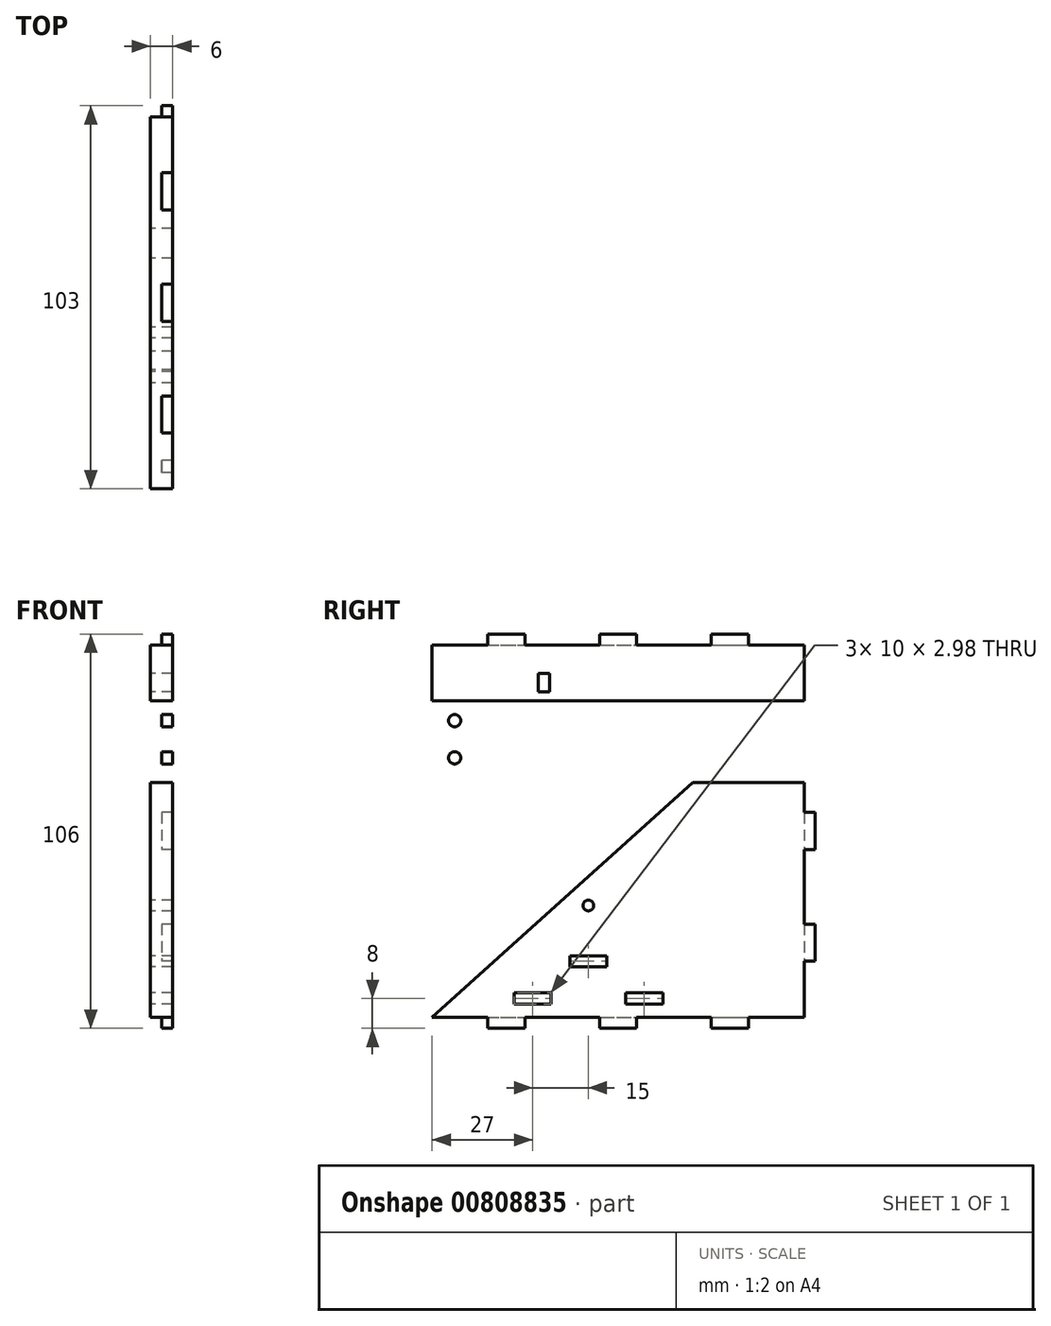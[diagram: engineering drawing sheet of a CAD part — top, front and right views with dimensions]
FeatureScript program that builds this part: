
annotation { "Feature Type Name" : "Feature", "Feature Type Description" : "" }
export const myFeature = defineFeature(function(context is Context, id is Id, definition is map)
    precondition{}
    {
        {
            var Q0;
            Q0=qCreatedBy(makeId("Right.planeOp"),FACE);
            var sketch = newSketch(context, id + "F0", { "sketchPlane" : qUnion([Q0])});
            skLineSegment(sketch, "E0.bottom", {"start": v(-50, 50) * mm, "end": v(50, 50) * mm});
            skLineSegment(sketch, "E0.top", {"start": v(-50, -50) * mm, "end": v(50, -50) * mm});
            skLineSegment(sketch, "E0.left", {"start": v(-50, 50) * mm, "end": v(-50, -50) * mm});
            skLineSegment(sketch, "E0.right", {"start": v(50, 50) * mm, "end": v(50, -50) * mm});
            skPoint(sketch, "E0.middle", {"position": v(0, 0) * mm});
            skLineSegment(sketch, "E1.bottom", {"start": v(-5, 47) * mm, "end": v(5, 47) * mm});
            skLineSegment(sketch, "E1.top", {"start": v(-5, 53) * mm, "end": v(5, 53) * mm});
            skLineSegment(sketch, "E1.left", {"start": v(-5, 47) * mm, "end": v(-5, 53) * mm});
            skLineSegment(sketch, "E1.right", {"start": v(5, 47) * mm, "end": v(5, 53) * mm});
            skPoint(sketch, "E1.middle", {"position": v(0, 50) * mm});
            skLineSegment(sketch, "E2.bottom", {"start": v(35, 53) * mm, "end": v(25, 53) * mm});
            skLineSegment(sketch, "E2.top", {"start": v(35, 47) * mm, "end": v(25, 47) * mm});
            skLineSegment(sketch, "E2.left", {"start": v(35, 53) * mm, "end": v(35, 47) * mm});
            skLineSegment(sketch, "E2.right", {"start": v(25, 53) * mm, "end": v(25, 47) * mm});
            skPoint(sketch, "E2.middle", {"position": v(30, 50) * mm});
            skLineSegment(sketch, "E3.bottom", {"start": v(-35, 53) * mm, "end": v(-25, 53) * mm});
            skLineSegment(sketch, "E3.top", {"start": v(-35, 47) * mm, "end": v(-25, 47) * mm});
            skLineSegment(sketch, "E3.left", {"start": v(-35, 53) * mm, "end": v(-35, 47) * mm});
            skLineSegment(sketch, "E3.right", {"start": v(-25, 53) * mm, "end": v(-25, 47) * mm});
            skPoint(sketch, "E3.middle", {"position": v(-30, 50) * mm});
            skLineSegment(sketch, "E4.1.0", {"start": v(-53, 25) * mm, "end": v(-47, 25) * mm});
            skLineSegment(sketch, "E4.1.1", {"start": v(-53, 35) * mm, "end": v(-53, 25) * mm});
            skLineSegment(sketch, "E4.1.2", {"start": v(-53, 35) * mm, "end": v(-47, 35) * mm});
            skLineSegment(sketch, "E4.1.3", {"start": v(-47, 35) * mm, "end": v(-47, 25) * mm});
            skLineSegment(sketch, "E4.1.4", {"start": v(-47, -5) * mm, "end": v(-47, 5) * mm});
            skLineSegment(sketch, "E4.1.5", {"start": v(-47, 5) * mm, "end": v(-53, 5) * mm});
            skLineSegment(sketch, "E4.1.6", {"start": v(-53, -5) * mm, "end": v(-53, 5) * mm});
            skLineSegment(sketch, "E4.1.7", {"start": v(-47, -5) * mm, "end": v(-53, -5) * mm});
            skLineSegment(sketch, "E4.1.8", {"start": v(-53, -35) * mm, "end": v(-53, -25) * mm});
            skLineSegment(sketch, "E4.1.9", {"start": v(-47, -35) * mm, "end": v(-47, -25) * mm});
            skLineSegment(sketch, "E4.1.10", {"start": v(-53, -25) * mm, "end": v(-47, -25) * mm});
            skLineSegment(sketch, "E4.1.11", {"start": v(-53, -35) * mm, "end": v(-47, -35) * mm});
            skLineSegment(sketch, "E4.2.0", {"start": v(-25, -53) * mm, "end": v(-25, -47) * mm});
            skLineSegment(sketch, "E4.2.1", {"start": v(-35, -53) * mm, "end": v(-25, -53) * mm});
            skLineSegment(sketch, "E4.2.2", {"start": v(-35, -53) * mm, "end": v(-35, -47) * mm});
            skLineSegment(sketch, "E4.2.3", {"start": v(-35, -47) * mm, "end": v(-25, -47) * mm});
            skLineSegment(sketch, "E4.2.4", {"start": v(5, -47) * mm, "end": v(-5, -47) * mm});
            skLineSegment(sketch, "E4.2.5", {"start": v(-5, -47) * mm, "end": v(-5, -53) * mm});
            skLineSegment(sketch, "E4.2.6", {"start": v(5, -53) * mm, "end": v(-5, -53) * mm});
            skLineSegment(sketch, "E4.2.7", {"start": v(5, -47) * mm, "end": v(5, -53) * mm});
            skLineSegment(sketch, "E4.2.8", {"start": v(35, -53) * mm, "end": v(25, -53) * mm});
            skLineSegment(sketch, "E4.2.9", {"start": v(35, -47) * mm, "end": v(25, -47) * mm});
            skLineSegment(sketch, "E4.2.10", {"start": v(25, -53) * mm, "end": v(25, -47) * mm});
            skLineSegment(sketch, "E4.2.11", {"start": v(35, -53) * mm, "end": v(35, -47) * mm});
            skLineSegment(sketch, "E4.3.0", {"start": v(53, -25) * mm, "end": v(47, -25) * mm});
            skLineSegment(sketch, "E4.3.1", {"start": v(53, -35) * mm, "end": v(53, -25) * mm});
            skLineSegment(sketch, "E4.3.2", {"start": v(53, -35) * mm, "end": v(47, -35) * mm});
            skLineSegment(sketch, "E4.3.3", {"start": v(47, -35) * mm, "end": v(47, -25) * mm});
            skLineSegment(sketch, "E4.3.4", {"start": v(47, 5) * mm, "end": v(47, -5) * mm});
            skLineSegment(sketch, "E4.3.5", {"start": v(47, -5) * mm, "end": v(53, -5) * mm});
            skLineSegment(sketch, "E4.3.6", {"start": v(53, 5) * mm, "end": v(53, -5) * mm});
            skLineSegment(sketch, "E4.3.7", {"start": v(47, 5) * mm, "end": v(53, 5) * mm});
            skLineSegment(sketch, "E4.3.8", {"start": v(53, 35) * mm, "end": v(53, 25) * mm});
            skLineSegment(sketch, "E4.3.9", {"start": v(47, 35) * mm, "end": v(47, 25) * mm});
            skLineSegment(sketch, "E4.3.10", {"start": v(53, 25) * mm, "end": v(47, 25) * mm});
            skLineSegment(sketch, "E4.3.11", {"start": v(53, 35) * mm, "end": v(47, 35) * mm});
            skCircle(sketch, "E5", {"center": v(-8, -20) * mm, "radius": 1.45 * mm});
            skSolve(sketch);
        }
        {
            var Q0;
            Q0=qSketchRegion(id+"F0",true);
            extrude(context, id + "F1", {"entities" : qUnion([Q0]), "depth" : 3 * mm, "offsetDistance" : 25 * mm});
        }
        {
            var Q0;
            Q0=makeQuery(id+"F1.opExtrude","CAP_FACE",FACE,{"disambiguationData":[OSD([sQuery(id+"F0.wireOp",EDGE,"E0.bottom"),sQuery(id+"F0.wireOp",EDGE,"E0.top"),sQuery(id+"F0.wireOp",EDGE,"E0.left"),sQuery(id+"F0.wireOp",EDGE,"E0.right"),sQuery(id+"F0.wireOp",EDGE,"E1.top"),sQuery(id+"F0.wireOp",EDGE,"E1.left"),sQuery(id+"F0.wireOp",EDGE,"E1.right"),sQuery(id+"F0.wireOp",EDGE,"E2.bottom"),sQuery(id+"F0.wireOp",EDGE,"E2.left"),sQuery(id+"F0.wireOp",EDGE,"E2.right"),sQuery(id+"F0.wireOp",EDGE,"E3.bottom"),sQuery(id+"F0.wireOp",EDGE,"E3.left"),sQuery(id+"F0.wireOp",EDGE,"E3.right"),sQuery(id+"F0.wireOp",EDGE,"E4.1.0"),sQuery(id+"F0.wireOp",EDGE,"E4.1.1"),sQuery(id+"F0.wireOp",EDGE,"E4.1.2"),sQuery(id+"F0.wireOp",EDGE,"E4.1.5"),sQuery(id+"F0.wireOp",EDGE,"E4.1.6"),sQuery(id+"F0.wireOp",EDGE,"E4.1.7"),sQuery(id+"F0.wireOp",EDGE,"E4.1.8"),sQuery(id+"F0.wireOp",EDGE,"E4.1.10"),sQuery(id+"F0.wireOp",EDGE,"E4.1.11"),sQuery(id+"F0.wireOp",EDGE,"E4.2.0"),sQuery(id+"F0.wireOp",EDGE,"E4.2.1"),sQuery(id+"F0.wireOp",EDGE,"E4.2.2"),sQuery(id+"F0.wireOp",EDGE,"E4.2.5"),sQuery(id+"F0.wireOp",EDGE,"E4.2.6"),sQuery(id+"F0.wireOp",EDGE,"E4.2.7"),sQuery(id+"F0.wireOp",EDGE,"E4.2.8"),sQuery(id+"F0.wireOp",EDGE,"E4.2.10"),sQuery(id+"F0.wireOp",EDGE,"E4.2.11"),sQuery(id+"F0.wireOp",EDGE,"E4.3.0"),sQuery(id+"F0.wireOp",EDGE,"E4.3.1"),sQuery(id+"F0.wireOp",EDGE,"E4.3.2"),sQuery(id+"F0.wireOp",EDGE,"E4.3.5"),sQuery(id+"F0.wireOp",EDGE,"E4.3.6"),sQuery(id+"F0.wireOp",EDGE,"E4.3.7"),sQuery(id+"F0.wireOp",EDGE,"E4.3.8"),sQuery(id+"F0.wireOp",EDGE,"E4.3.10"),sQuery(id+"F0.wireOp",EDGE,"E4.3.11")])],"isStart":true});
            var sketch = newSketch(context, id + "F2", { "sketchPlane" : qUnion([Q0])});
            skLineSegment(sketch, "E6", {"start": v(-50, -50) * mm, "end": v(50, -50) * mm});
            skLineSegment(sketch, "E7", {"start": v(50, -50) * mm, "end": v(-20, 13) * mm});
            skLineSegment(sketch, "E8", {"start": v(-20, 13) * mm, "end": v(-50, 13) * mm});
            skLineSegment(sketch, "E9", {"start": v(-50, 13) * mm, "end": v(-50, -50) * mm});
            skLineSegment(sketch, "E10", {"start": v(0, 0) * mm, "end": v(0, 15) * mm});
            skLineSegment(sketch, "E11", {"start": v(-50, 35) * mm, "end": v(50, 35) * mm});
            skLineSegment(sketch, "E12", {"start": v(50, 50) * mm, "end": v(-50, 50) * mm});
            skLineSegment(sketch, "E13", {"start": v(-50, 50) * mm, "end": v(-50, 35) * mm});
            skLineSegment(sketch, "E14", {"start": v(50, 35) * mm, "end": v(50, 50) * mm});
            skLineSegment(sketch, "E15.top", {"start": v(0, 34.4) * mm, "end": v(39.9, 34.4) * mm});
            skLineSegment(sketch, "E15.left", {"start": v(0, 15) * mm, "end": v(0, 34.4) * mm});
            skLineSegment(sketch, "E15.right", {"start": v(39.9, 15) * mm, "end": v(39.9, 34.4) * mm});
            skLineSegment(sketch, "E16", {"start": v(0, 24.7) * mm, "end": v(39.9, 24.7) * mm, "construction": true});
            skLineSegment(sketch, "E17", {"start": v(19.95, 34.4) * mm, "end": v(19.95, 15) * mm, "construction": true});
            skLineSegment(sketch, "E18.MirrorCS", {"start": v(39.9, 15) * mm, "end": v(0, 15) * mm});
            skCircle(sketch, "E19", {"center": v(-4.05, 29.7) * mm, "radius": 1.65 * mm});
            skCircle(sketch, "E20.0.1.0", {"center": v(-4.05, 19.7) * mm, "radius": 1.65 * mm});
            skLineSegment(sketch, "E20.direction1", {"start": v(-4.05, 29.7) * mm, "end": v(20.95, 29.7) * mm, "construction": true});
            skLineSegment(sketch, "E20.direction2", {"start": v(-4.05, 29.7) * mm, "end": v(-4.05, 19.7) * mm, "construction": true});
            skCircle(sketch, "E21.MirrorC", {"center": v(43.95, 29.7) * mm, "radius": 1.65 * mm});
            skCircle(sketch, "E22.MirrorC", {"center": v(43.95, 19.7) * mm, "radius": 1.65 * mm});
            skLineSegment(sketch, "E23.MirrorCS", {"start": v(43.95, 29.7) * mm, "end": v(43.95, 19.7) * mm, "construction": true});
            skLineSegment(sketch, "E24.MirrorCS", {"start": v(43.95, 29.7) * mm, "end": v(18.95, 29.7) * mm, "construction": true});
            skLineSegment(sketch, "E25", {"start": v(9.98, 15) * mm, "end": v(9.98, 12) * mm, "construction": true});
            skLineSegment(sketch, "E26.bottom", {"start": v(9.98, 12) * mm, "end": v(12.96, 12) * mm});
            skLineSegment(sketch, "E26.top", {"start": v(9.98, 7) * mm, "end": v(12.96, 7) * mm});
            skLineSegment(sketch, "E26.left", {"start": v(9.98, 12) * mm, "end": v(9.98, 7) * mm});
            skLineSegment(sketch, "E26.right", {"start": v(12.96, 12) * mm, "end": v(12.96, 7) * mm});
            skLineSegment(sketch, "E27.MirrorCS", {"start": v(29.92, 15) * mm, "end": v(29.92, 12) * mm, "construction": true});
            skLineSegment(sketch, "E28.MirrorCS", {"start": v(29.92, 7) * mm, "end": v(26.94, 7) * mm});
            skLineSegment(sketch, "E29.MirrorCS", {"start": v(29.92, 12) * mm, "end": v(29.92, 7) * mm});
            skLineSegment(sketch, "E30.MirrorCS", {"start": v(26.94, 12) * mm, "end": v(26.94, 7) * mm});
            skLineSegment(sketch, "E31.MirrorCS", {"start": v(29.92, 12) * mm, "end": v(26.94, 12) * mm});
            skLineSegment(sketch, "E32", {"start": v(19.95, 34.4) * mm, "end": v(19.95, 37.4) * mm, "construction": true});
            skLineSegment(sketch, "E33.bottom", {"start": v(18.46, 37.4) * mm, "end": v(21.44, 37.4) * mm});
            skLineSegment(sketch, "E33.top", {"start": v(18.46, 42.4) * mm, "end": v(21.44, 42.4) * mm});
            skLineSegment(sketch, "E33.left", {"start": v(18.46, 37.4) * mm, "end": v(18.46, 42.4) * mm});
            skLineSegment(sketch, "E33.right", {"start": v(21.44, 37.4) * mm, "end": v(21.44, 42.4) * mm});
            skSolve(sketch);
        }
        {
            var Q0;
            Q0=makeQuery(id+"F2.imprint","IMPRINT",FACE,{"disambiguationData":[TD([[makeQuery(id+"F2.imprint","IMPRINT",EDGE,{"derivedFrom":sQuery(id+"F2.wireOp",EDGE,"E19")}),1.0]])]});
            var Q1;
            Q1=makeQuery(id+"F2.imprint","IMPRINT",FACE,{"disambiguationData":[TD([[makeQuery(id+"F2.imprint","IMPRINT",EDGE,{"derivedFrom":sQuery(id+"F2.wireOp",EDGE,"E20.0.1.0")}),1.0]])]});
            var Q2;
            Q2=makeQuery(id+"F2.imprint","IMPRINT",FACE,{"disambiguationData":[TD([[makeQuery(id+"F2.imprint","IMPRINT",EDGE,{"derivedFrom":sQuery(id+"F2.wireOp",EDGE,"E21.MirrorC")}),-1.0]])]});
            var Q3;
            Q3=makeQuery(id+"F2.imprint","IMPRINT",FACE,{"disambiguationData":[TD([[makeQuery(id+"F2.imprint","IMPRINT",EDGE,{"derivedFrom":sQuery(id+"F2.wireOp",EDGE,"E22.MirrorC")}),-1.0]])]});
            var Q4;
            Q4=makeQuery(id+"F2.imprint","IMPRINT",FACE,{"disambiguationData":[TD([[makeQuery(id+"F2.imprint","IMPRINT",EDGE,{"derivedFrom":sQuery(id+"F2.wireOp",EDGE,"E26.bottom")}),-1.0]])]});
            var Q5;
            Q5=makeQuery(id+"F2.imprint","IMPRINT",FACE,{"disambiguationData":[TD([[makeQuery(id+"F2.imprint","IMPRINT",EDGE,{"derivedFrom":sQuery(id+"F2.wireOp",EDGE,"E28.MirrorCS")}),-1.0]])]});
            var Q6;
            Q6=makeQuery(id+"F2.imprint","IMPRINT",FACE,{"disambiguationData":[TD([[makeQuery(id+"F2.imprint","IMPRINT",EDGE,{"derivedFrom":sQuery(id+"F2.wireOp",EDGE,"E15.top")}),-1.0]])]});
            var Q7;
            Q7=makeQuery(id+"F2.imprint","IMPRINT",FACE,{"disambiguationData":[TD([[makeQuery(id+"F2.imprint","IMPRINT",EDGE,{"derivedFrom":sQuery(id+"F2.wireOp",EDGE,"E33.bottom")}),1.0]])]});
            extrude(context, id + "F3", {"entities" : qUnion([Q0, Q1, Q2, Q3, Q4, Q5, Q6, Q7]), "operationType" : NewBodyOperationType.REMOVE, "oppositeDirection" : true, "depth" : 25 * mm, "offsetDistance" : 25 * mm});
        }
        {
            var Q0;
            Q0=makeQuery(id+"F2.imprint","IMPRINT",FACE,{"disambiguationData":[TD([[makeQuery(id+"F2.imprint","IMPRINT",EDGE,{"derivedFrom":sQuery(id+"F2.wireOp",EDGE,"E11")}),1.0]])]});
            var Q1;
            {var subQ5=sQuery(id+"F2.wireOp",EDGE,"E7");Q1=makeQuery(id+"F2.imprint","IMPRINT",FACE,{"disambiguationData":[TD([[makeQuery(id+"F2.imprint","IMPRINT",EDGE,{"derivedFrom":subQ5}),1.0]])]});}
            extrude(context, id + "F4", {"entities" : qUnion([Q0, Q1]), "operationType" : NewBodyOperationType.ADD, "depth" : 3 * mm, "offsetDistance" : 25 * mm});
        }
        {
            var Q0;
            Q0=qCreatedBy(makeId("Right.planeOp"),FACE);
            var sketch = newSketch(context, id + "F5", { "sketchPlane" : qUnion([Q0])});
            skLineSegment(sketch, "E34.bottom", {"start": v(-50, -50) * mm, "end": v(50, -50) * mm});
            skLineSegment(sketch, "E34.top", {"start": v(-50, 50) * mm, "end": v(50, 50) * mm});
            skLineSegment(sketch, "E34.left", {"start": v(-50, -50) * mm, "end": v(-50, 50) * mm});
            skPoint(sketch, "E34.middle", {"position": v(0, 0) * mm});
            skLineSegment(sketch, "E35.bottom", {"start": v(2, -46.5) * mm, "end": v(12, -46.5) * mm});
            skLineSegment(sketch, "E35.top", {"start": v(2, -43.51) * mm, "end": v(12, -43.51) * mm});
            skLineSegment(sketch, "E35.left", {"start": v(2, -46.5) * mm, "end": v(2, -43.51) * mm});
            skLineSegment(sketch, "E35.right", {"start": v(12, -46.5) * mm, "end": v(12, -43.51) * mm});
            skPoint(sketch, "E35.middle", {"position": v(7, -45) * mm});
            skLineSegment(sketch, "E36.bottom", {"start": v(-28, -46.5) * mm, "end": v(-18, -46.5) * mm});
            skLineSegment(sketch, "E36.top", {"start": v(-28, -43.51) * mm, "end": v(-18, -43.51) * mm});
            skLineSegment(sketch, "E36.left", {"start": v(-28, -46.5) * mm, "end": v(-28, -43.51) * mm});
            skLineSegment(sketch, "E36.right", {"start": v(-18, -46.5) * mm, "end": v(-18, -43.51) * mm});
            skPoint(sketch, "E36.middle", {"position": v(-23, -45) * mm});
            skLineSegment(sketch, "E37.bottom", {"start": v(-3, -36.5) * mm, "end": v(-13, -36.5) * mm});
            skLineSegment(sketch, "E37.top", {"start": v(-3, -33.51) * mm, "end": v(-13, -33.51) * mm});
            skLineSegment(sketch, "E37.left", {"start": v(-3, -36.5) * mm, "end": v(-3, -33.51) * mm});
            skLineSegment(sketch, "E37.right", {"start": v(-13, -36.5) * mm, "end": v(-13, -33.51) * mm});
            skPoint(sketch, "E37.middle", {"position": v(-8, -35) * mm});
            skSolve(sketch);
        }
        {
            var Q0;
            Q0=qSketchRegion(id+"F5",true);
            extrude(context, id + "F6", {"entities" : qUnion([Q0]), "operationType" : NewBodyOperationType.REMOVE, "depth" : 25 * mm, "offsetDistance" : 25 * mm, "symmetric" : true});
        }
    });
